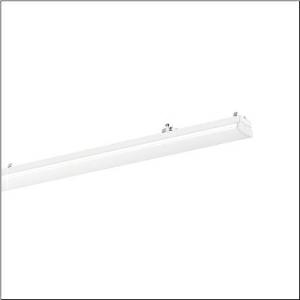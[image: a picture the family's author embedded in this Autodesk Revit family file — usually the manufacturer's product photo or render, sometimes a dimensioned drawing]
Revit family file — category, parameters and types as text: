
# Revit family: licross_r__21_recessed_opal_mo_52te1dvn48xg_49a0
name_source: partatom
category: Lighting Fixtures
units: mm (PartAtom-declared; Revit-internal decimal feet)

## family parameters
Cut with Voids When Loaded = No
Host = Face
Light Source = No
Part Type = Normal
Room Calculation Point = No
Round Connector Dimension = Use Diameter
Shared = No

## types (1)
- --- (1 x LED, 8000 lm, 46.8 W, 4000K)
    Apparent Load = 47 VA
    CIE Flux Codes = 44 73 91 87 100
    Color Rendering = 80
    Color Temperature = 4000K
    Default Elevation = 1800 mm
    Description = Licross® 21 recessed opal MO, luminaire insert, of sheet steel, galvanised, coil coated, white, length: 1.500mm, width: 66mm, height: 67mm, LED rated luminous flux: 8.000lm, light colour: 840, control gear: DALI 2, CLO, with plug, 5-pole, with phase selection, mains connection: 220..240V, AC, 50/60Hz, start of lifetime: 47W, end of service life: 56W, internal wiring halogen-free, primary optical cover: cover, of PMMA, light emission: direct with ceiling illumination distribution, primary light characteristic: symmetric, protection rating (complete): IP54, insulation class (complete): insulation class I (protective earthing), certification: CE, ENEC, VDE, UKCA, protection symbol: D if used in an environment with non-conductive dust loads with corresponding accessories, impact resistance: IK06, permissible ambient temperature for indoor applications: -25..+35°C, corresponds to IFS (International Featured Standards) requirements for safety and quality in the food industry, reducing of maximum allowable ambient temperature of 5°C with ceiling mounting, LABS conformity tested according to VDMA 24364:2018-05, packaging unit: 1 piece
    Height = 83 mm
    Lamp = 1 x LED
    Lamp Light Flux = 8000 lm
    Lamp Power = 46.8 W
    Lamp count = 1
    Length = 1500 mm
    Luminous efficacy = 171 lm/W
    Manufacturer = Siteco
    ModVariant = No
    Model = 52TE1DVN48XG
    Mounting Place = Ceiling
    Mounting Type = Pendant
    Number of Poles = 1
    OnlyDefault = Yes
    Power Factor = 1
    Product Name = Licross® 21 recessed opal MO
    Product group = luminaire insert | ceiling pendant
    ProductGroupID = 902
    Protection Class = Protection class I
    Protection Degree = IP 54
    RLX_Detail_Level = 1
    RLX_Emergency_Light_Flux = 0 lm
    RLX_Emergency_Type = 0
    RLX_Emergency_Type_DB = No
    RlxData = <blob elided: 26801 chars, md5=249ed024>
    Socket = socket
    Standby Power = 0 W
    System Light Flux = 8000 lm
    System Power = 47 W
    Type Comments = factory setting: luminous flux: 100 % | dim-lin: 254 | 315 mA
    Type Image = l_1313666.jpg
    URL = http://relux.com
    VarID = @adj_089803
    Voltage = 0 V
    Weight = 0.00 kg
    Width = 76 mm

## geometry (parser evidence)
native form markers: Blend x4, Sweep x13
no freeform markers — native parametric forms only
